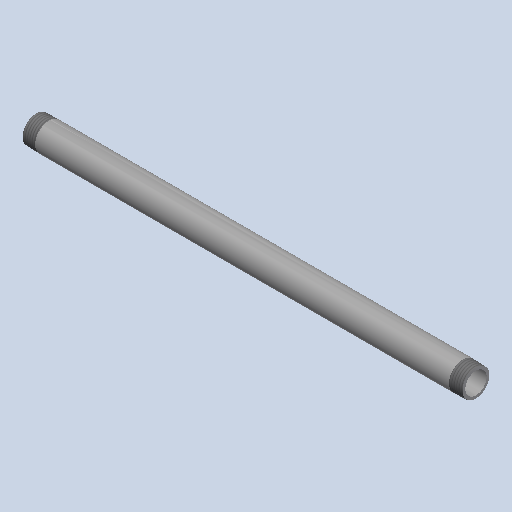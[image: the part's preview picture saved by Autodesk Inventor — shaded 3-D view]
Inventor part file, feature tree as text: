
AUTODESK INVENTOR PART (.ipt)
format: ipt  version: 2025 (Build 290162000, 162)  size: 159,232 bytes
history: native  units: mm (DEFAULTED — no unit token found)
features: other x8, revolve x1
ambient origin geometry x8: Origin, YZ Plane, XZ Plane, XY Plane, X Axis, Y Axis, Z Axis, Center Point
bodies: Solid1 (feature_tree)
feature tree (9):
  revolve  "Revolution1"  [1 undecoded]
  other  "Work Axis1"
  other  "Work Point5"
  other  "Work Axis2"
  other  "Work Point6"
  other  "Work Axis3"
  other  "Work Axis4"
  other  "Work Point7"
  other  "Work Point8"
note: 1 required parameter value undecoded (feature->parameter linkage not recoverable at this tier; creation-order binding heuristic only, values carry confidence <= 0.55)
